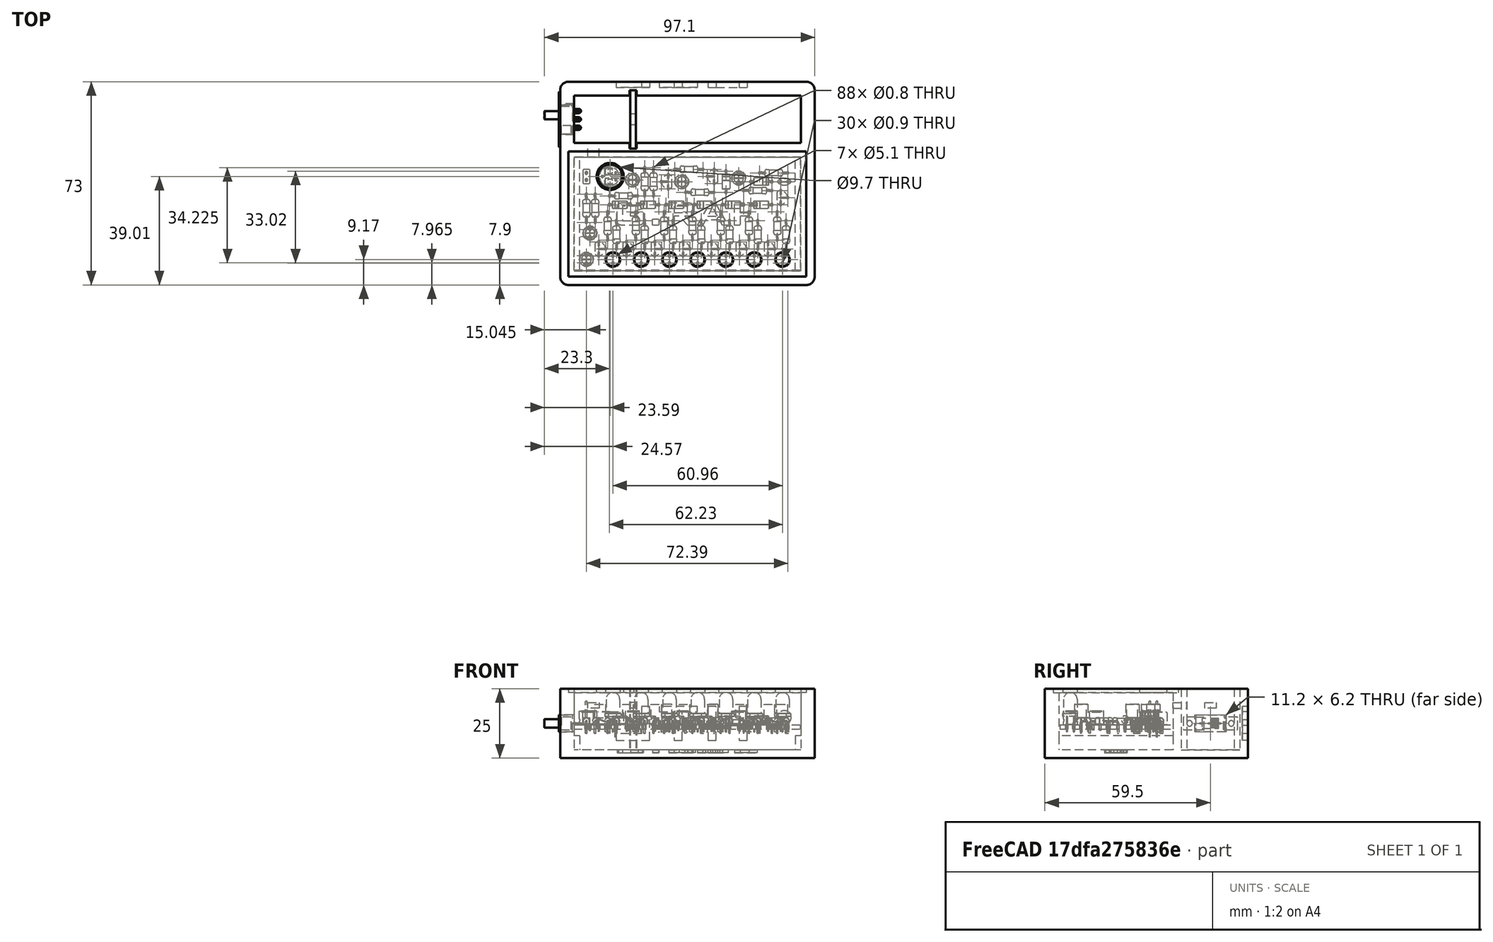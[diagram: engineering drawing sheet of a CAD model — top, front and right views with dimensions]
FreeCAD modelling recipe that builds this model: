
FCSTD DOCUMENT  (FreeCAD 0.20R29177 +426 (Git))
Label: housing
License: All rights reserved
LicenseURL: http://en.wikipedia.org/wiki/All_rights_reserved
objects: Part::Feature×64, TechDraw::DrawViewDimension×22, Sketcher::SketchObject×12, PartDesign::Pocket×10, App::Part×9, App::DocumentObjectGroupPython×4, PartDesign::Pad×3, PartDesign::Body×3, TechDraw::DrawSVGTemplate×3, TechDraw::DrawPage×3, TechDraw::DrawProjGroupItem×3, Part::Part2DObjectPython×2, TechDraw::DrawViewSpreadsheet×2, TechDraw::DrawViewPart×2, Spreadsheet::Sheet×1, TechDraw::DrawProjGroup×1, PartDesign::CoordinateSystem×1
note: 108 computed .brp shape members not serialized (recipe doc carries the construction recipe); baked Part::Feature solids carry a one-line shape summary decoded from their .brp

FEATURE [Spreadsheet::Sheet] Spreadsheet  label="Parameter"
  cells = A1=Board_Width; B1(Board_Width)=81.5; C1(Board_Length)=41; F1=Size; A2=Battery_Size; B2(Battery_Size)=17; E2=2AA_V; F2=16.5; A3=Height; B3(Height)=25; E3=2AA_H; F3=26; A4=Border; B4(Border)=5; E4=6AA_V; F4=47.5; A5=Border_Radius; B5(Border_Radius)=3; E5=6AA_H; F5=37.5; A6=Offset; B6(Offset)=-12; E6=6AAA_V; F6=26.2; A7=Overlay; B7(Overlay_Width)=2; C7(Overlay_Length)=0; E7=6AAA_H; F7=37.5; A8=Floor_Thickness; B8(Floor_Thickness)=3; E8=9VBLOCK_V; F8=17; A9=Base_Height; B9(Base_Height)=5; E9=9V_BLOCK_H; F9=26; A10=Inlay_Frame; B10(Inlay_Frame)=2; E10=Manual; F10=10; A11=Inlay_Height; B11(Inlay_Height)=1.5; C11=DICK; A12=Power_Size; B12(Power_Width)=4; C12(Power_Length)=2; A13=Power_Position; B13(Power_X)=5; C13(Power_Y)=6; A14=Power_Separation; B14(Power_Separation)=20; C14(Power_Separation_Size)=2; D14=DICK; A15=Power_Tolerance; B15(Power_Tolerance)=0.5; A16=Switch_Size; B16(Switch_Width)=11.2; C16(Switch_Height)=6.2; A17=Switch_Position; B17(Switch_X)==Border + Battery_Size / 2 - Switch_Width / 2; C17(Switch_Y)==Height / 2 + Offset - Switch_Height / 2; A18=Text; B18(Text)=HTL; C18(Text_Size)==Board_Width * (1 - 0.4) / Text_Length > Height * (1 - 0.2) ? Height * (1 - 0.2) : Board_Width * (1 - 0.4) / Text_Length; D18(Text_Length)=3; E18=Zeichen; A19=Text_Position; B19(Text_X)==Board_Width / 2 + Text_Length / 2 * Text_Size; C19(Text_Y)==Height / 2 + Offset - Text_Height / 2; A20=Text_Height; B20(Text_Height)==0.747 * Text_Size; A21=Text_Author; B21(Text_Author)=G.RAF; C21(Text_Author_Size)==Board_Width * (1 - 0.6) / Text_Length > Board_Length * (1 - 0.4) ? Board_Length * (1 - 0.4) : Board_Width * (1 - 0.6) / Text_Length; D21(Text_Author_Length)=5; E21=Zeichen; A22=Text_Author_Position; B22(Text_Author_X)==Board_Width / 2 - Text_Author_Length / 2 * Text_Author_Size; C22(Text_Author_Y)==-Board_Length / 2 - Text_Author_Height / 2; A23=Text_Author_Size; B23(Text_Author_Height)==0.747 * Text_Author_Size
FEATURE [Sketcher::SketchObject] Sketch
  AttachmentOffset = pos=(0,0,-12) rot=(0,0,1;0rad)
  FullyConstrained = true
  MapMode = 5
  Placement = pos=(0,0,-12) rot=(0,0,1;0rad)
  Support = -> [XY_Plane001]
  expr: .AttachmentOffset.Base.z = <<Parameter>>.Offset
  expr: Constraints[14] = <<Parameter>>.Board_Width + 2 * <<Parameter>>.Border
  expr: Constraints[15] = <<Parameter>>.Board_Length + <<Parameter>>.Border
  expr: Constraints[19] = <<Parameter>>.Border_Radius
  expr: Constraints[6] = <<Parameter>>.Battery_Size + 2 * <<Parameter>>.Border
  expr: Constraints[7] = <<Parameter>>.Border
  sketch-geometry (8):
    g0: LineSegment StartX=-2 StartY=27 StartZ=0 EndX=83.5 EndY=27 EndZ=0
    g1: LineSegment StartX=86.5 StartY=24 StartZ=0 EndX=86.5 EndY=-43 EndZ=0
    g2: LineSegment StartX=83.5 StartY=-46 StartZ=0 EndX=-2 EndY=-46 EndZ=0
    g3: LineSegment StartX=-5 StartY=-43 StartZ=0 EndX=-5 EndY=24 EndZ=0
    g4: ArcOfCircle CenterX=-2 CenterY=24 CenterZ=0 NormalX=0 NormalY=0 NormalZ=1 AngleXU=0 Radius=3 StartAngle=1.5708 EndAngle=3.14159
    g5: ArcOfCircle CenterX=83.5 CenterY=24 CenterZ=0 NormalX=0 NormalY=0 NormalZ=1 AngleXU=0 Radius=3 StartAngle=1.508e-13 EndAngle=1.5708
    g6: ArcOfCircle CenterX=83.5 CenterY=-43 CenterZ=0 NormalX=0 NormalY=0 NormalZ=1 AngleXU=0 Radius=3 StartAngle=4.71239 EndAngle=6.28319
    g7: ArcOfCircle CenterX=-2 CenterY=-43 CenterZ=0 NormalX=0 NormalY=0 NormalZ=1 AngleXU=0 Radius=3 StartAngle=3.14159 EndAngle=4.71239
  constraints (20):
    c: Horizontal(g0)
    c: Horizontal(g2)
    c: Vertical(g1)
    c: Vertical(g3)
    c: Tangent(g0,g4) = 1.5708
    c: Tangent(g3,g4) = 1.5708
    c: DistanceY(g-1,g0) = 27
    c: DistanceX(g3,g-1) = 5
    c: Tangent(g0,g5) = 1.5708
    c: Tangent(g1,g5) = 1.5708
    c: Tangent(g1,g6) = 1.5708
    c: Tangent(g2,g6) = 1.5708
    c: Tangent(g2,g7) = 1.5708
    c: Tangent(g3,g7) = 1.5708
    c: DistanceX(g3,g1) = 91.5
    c: DistanceY(g2,g-1) = 46
    c: Equal(g4,g5)
    c: Equal(g5,g6)
    c: Equal(g6,g7)
    c: Radius(g4) = 3
FEATURE [PartDesign::Pad] Pad
  Direction = (0,0,1)
  Length = 25
  Length2 = 10
  Profile = -> Sketch
  ReferenceAxis = -> Sketch [N_Axis]
  Type = 0
  expr: Length = <<Parameter>>.Height
FEATURE [Sketcher::SketchObject] Sketch001
  AttachmentOffset = pos=(0,0,13) rot=(0,0,1;0rad)
  FullyConstrained = true
  MapMode = 5
  Placement = pos=(0,0,13) rot=(0,0,1;0rad)
  Support = -> [XY_Plane001]
  expr: .AttachmentOffset.Base.z = <<Parameter>>.Height + <<Parameter>>.Offset
  expr: .AttachmentOffset.Rotation.Yaw = 0
  expr: Constraints[10] = <<Parameter>>.Overlay_Width
  expr: Constraints[11] = <<Parameter>>.Board_Width - 2 * <<Parameter>>.Overlay_Width
  expr: Constraints[21] = <<Parameter>>.Border
  expr: Constraints[22] = <<Parameter>>.Battery_Size
  expr: Constraints[23] = <<Parameter>>.Board_Width
  expr: Constraints[8] = <<Parameter>>.Overlay_Length
  expr: Constraints[9] = <<Parameter>>.Board_Length - 2 * <<Parameter>>.Overlay_Length
  sketch-geometry (8):
    g0: LineSegment StartX=2 StartY=0 StartZ=0 EndX=79.5 EndY=0 EndZ=0
    g1: LineSegment StartX=79.5 StartY=0 StartZ=0 EndX=79.5 EndY=-41 EndZ=0
    g2: LineSegment StartX=79.5 StartY=-41 StartZ=0 EndX=2 EndY=-41 EndZ=0
    g3: LineSegment StartX=2 StartY=-41 StartZ=0 EndX=2 EndY=0 EndZ=0
    g4: LineSegment StartX=0 StartY=22 StartZ=0 EndX=81.5 EndY=22 EndZ=0
    g5: LineSegment StartX=81.5 StartY=22 StartZ=0 EndX=81.5 EndY=5 EndZ=0
    g6: LineSegment StartX=81.5 StartY=5 StartZ=0 EndX=0 EndY=5 EndZ=0
    g7: LineSegment StartX=0 StartY=5 StartZ=0 EndX=0 EndY=22 EndZ=0
  constraints (24):
    c: Coincident(g0,g1)
    c: Coincident(g1,g2)
    c: Coincident(g2,g3)
    c: Coincident(g3,g0)
    c: Horizontal(g0)
    c: Horizontal(g2)
    c: Vertical(g1)
    c: Vertical(g3)
    c: DistanceY(g0,g-1) = 0
    c: DistanceY(g3,g3) = 41
    c: DistanceX(g-1,g0) = 2
    c: DistanceX(g0,g0) = 77.5
    c: Coincident(g4,g5)
    c: Coincident(g5,g6)
    c: Coincident(g6,g7)
    c: Coincident(g7,g4)
    c: Horizontal(g4)
    c: Horizontal(g6)
    c: Vertical(g5)
    c: Vertical(g7)
    c: PointOnObject(g4,g-2)
    c: DistanceY(g-1,g6) = 5
    c: DistanceY(g6,g4) = 17
    c: DistanceX(g4,g4) = 81.5
FEATURE [PartDesign::Pocket] Pocket
  BaseFeature = -> Pad
  Direction = (0,0,-1)
  Length = 22
  Length2 = 5
  Profile = -> Sketch001
  ReferenceAxis = -> Sketch001 [N_Axis]
  Type = 0
  expr: Length = <<Parameter>>.Height - <<Parameter>>.Floor_Thickness
FEATURE [Sketcher::SketchObject] Sketch002
  AttachmentOffset = pos=(0,0,13) rot=(0,0,1;0rad)
  FullyConstrained = true
  MapMode = 5
  Placement = pos=(0,0,13) rot=(0,0,1;0rad)
  Support = -> [XY_Plane001]
  expr: .AttachmentOffset.Base.z = <<Parameter>>.Height + <<Parameter>>.Offset
  expr: Constraints[10] = <<Parameter>>.Board_Length
  expr: Constraints[9] = <<Parameter>>.Board_Width
  sketch-geometry (4):
    g0: LineSegment StartX=0 StartY=0 StartZ=0 EndX=81.5 EndY=0 EndZ=0
    g1: LineSegment StartX=81.5 StartY=0 StartZ=0 EndX=81.5 EndY=-41 EndZ=0
    g2: LineSegment StartX=81.5 StartY=-41 StartZ=0 EndX=0 EndY=-41 EndZ=0
    g3: LineSegment StartX=0 StartY=-41 StartZ=0 EndX=0 EndY=0 EndZ=0
  constraints (11):
    c: Coincident(g0,g1)
    c: Coincident(g1,g2)
    c: Coincident(g2,g3)
    c: Coincident(g3,g0)
    c: Horizontal(g0)
    c: Horizontal(g2)
    c: Vertical(g1)
    c: Vertical(g3)
    c: Coincident(g0,g-1)
    c: DistanceX(g0,g0) = 81.5
    c: DistanceY(g3,g3) = 41
FEATURE [PartDesign::Pocket] Pocket001
  BaseFeature = -> Pocket
  Direction = (0,0,-1)
  Length = 17
  Length2 = 5
  Profile = -> Sketch002
  ReferenceAxis = -> Sketch002 [N_Axis]
  Type = 0
  expr: Length = <<Parameter>>.Height - <<Parameter>>.Floor_Thickness - <<Parameter>>.Base_Height
FEATURE [Sketcher::SketchObject] Sketch003
  AttachmentOffset = pos=(0,0,13) rot=(0,0,1;0rad)
  FullyConstrained = true
  MapMode = 5
  Placement = pos=(0,0,13) rot=(0,0,1;0rad)
  Support = -> [XY_Plane001]
  expr: .AttachmentOffset.Base.z = <<Parameter>>.Height + <<Parameter>>.Offset
  expr: Constraints[10] = <<Parameter>>.Board_Length + 2 * <<Parameter>>.Inlay_Frame
  expr: Constraints[11] = <<Parameter>>.Board_Width + 2 * <<Parameter>>.Inlay_Frame
  expr: Constraints[8] = <<Parameter>>.Inlay_Frame
  expr: Constraints[9] = <<Parameter>>.Inlay_Frame
  sketch-geometry (4):
    g0: LineSegment StartX=-2 StartY=2 StartZ=0 EndX=83.5 EndY=2 EndZ=0
    g1: LineSegment StartX=83.5 StartY=2 StartZ=0 EndX=83.5 EndY=-43 EndZ=0
    g2: LineSegment StartX=83.5 StartY=-43 StartZ=0 EndX=-2 EndY=-43 EndZ=0
    g3: LineSegment StartX=-2 StartY=-43 StartZ=0 EndX=-2 EndY=2 EndZ=0
  constraints (12):
    c: Coincident(g0,g1)
    c: Coincident(g1,g2)
    c: Coincident(g2,g3)
    c: Coincident(g3,g0)
    c: Horizontal(g0)
    c: Horizontal(g2)
    c: Vertical(g1)
    c: Vertical(g3)
    c: DistanceX(g0,g-1) = 2
    c: DistanceY(g-1,g0) = 2
    c: DistanceY(g1,g0) = 45
    c: DistanceX(g2,g1) = 85.5
FEATURE [PartDesign::Pocket] Pocket002
  BaseFeature = -> Pocket001
  Direction = (0,0,-1)
  Length = 1.5
  Length2 = 5
  Profile = -> Sketch003
  ReferenceAxis = -> Sketch003 [N_Axis]
  Refine = true
  Type = 0
  expr: Length = <<Parameter>>.Inlay_Height
FEATURE [Sketcher::SketchObject] Sketch004
  FullyConstrained = true
  MapMode = 5
  Placement = pos=(0,0,0) rot=(1,0,0;1.5708rad)
  Support = -> [XZ_Plane001]
  expr: Constraints[10] = <<Parameter>>.Power_Length
  expr: Constraints[11] = <<Parameter>>.Power_Width
  expr: Constraints[8] = <<Parameter>>.Power_X
  expr: Constraints[9] = <<Parameter>>.Power_Y
  sketch-geometry (4):
    g0: LineSegment StartX=5 StartY=8 StartZ=0 EndX=9 EndY=8 EndZ=0
    g1: LineSegment StartX=9 StartY=8 StartZ=0 EndX=9 EndY=6 EndZ=0
    g2: LineSegment StartX=9 StartY=6 StartZ=0 EndX=5 EndY=6 EndZ=0
    g3: LineSegment StartX=5 StartY=6 StartZ=0 EndX=5 EndY=8 EndZ=0
  constraints (12):
    c: Coincident(g0,g1)
    c: Coincident(g1,g2)
    c: Coincident(g2,g3)
    c: Coincident(g3,g0)
    c: Horizontal(g0)
    c: Horizontal(g2)
    c: Vertical(g1)
    c: Vertical(g3)
    c: DistanceX(g-1,g2) = 5
    c: DistanceY(g-1,g2) = 6
    c: DistanceY(g3,g3) = 2
    c: DistanceX(g0,g0) = 4
FEATURE [PartDesign::Pocket] Pocket003
  BaseFeature = -> Pocket002
  Direction = (0,1,2e-16)
  Length = 5
  Length2 = 5
  Profile = -> Sketch004
  ReferenceAxis = -> Sketch004 [N_Axis]
  Refine = true
  Type = 0
  expr: Length = <<Parameter>>.Border
FEATURE [Sketcher::SketchObject] Sketch005
  FullyConstrained = true
  MapMode = 5
  Placement = pos=(0,0,0) rot=(0.57735,0.57735,0.57735;2.0944rad)
  Support = -> [YZ_Plane001]
  expr: Constraints[10] = <<Parameter>>.Switch_X
  expr: Constraints[11] = <<Parameter>>.Switch_Y
  expr: Constraints[8] = <<Parameter>>.Switch_Width
  expr: Constraints[9] = <<Parameter>>.Switch_Height
  sketch-geometry (4):
    g0: LineSegment StartX=7.9 StartY=3.6 StartZ=0 EndX=19.1 EndY=3.6 EndZ=0
    g1: LineSegment StartX=19.1 StartY=3.6 StartZ=0 EndX=19.1 EndY=-2.6 EndZ=0
    g2: LineSegment StartX=19.1 StartY=-2.6 StartZ=0 EndX=7.9 EndY=-2.6 EndZ=0
    g3: LineSegment StartX=7.9 StartY=-2.6 StartZ=0 EndX=7.9 EndY=3.6 EndZ=0
  constraints (12):
    c: Coincident(g0,g1)
    c: Coincident(g1,g2)
    c: Coincident(g2,g3)
    c: Coincident(g3,g0)
    c: Horizontal(g0)
    c: Horizontal(g2)
    c: Vertical(g1)
    c: Vertical(g3)
    c: DistanceX(g0,g0) = 11.2
    c: DistanceY(g1,g1) = 6.2
    c: DistanceX(g-1,g2) = 7.9
    c: DistanceY(g-1,g2) = -2.6
FEATURE [PartDesign::Pocket] Pocket004
  BaseFeature = -> Pocket003
  Direction = (-1,2e-16,-3e-16)
  Length = 5
  Length2 = 5
  Profile = -> Sketch005
  ReferenceAxis = -> Sketch005 [N_Axis]
  Refine = true
  Type = 0
  expr: Length = <<Parameter>>.Border
FEATURE [Sketcher::SketchObject] Sketch006
  AttachmentOffset = pos=(0,0,13) rot=(0,0,1;0rad)
  FullyConstrained = true
  MapMode = 5
  Placement = pos=(0,0,13) rot=(0,0,1;0rad)
  Support = -> [XY_Plane001]
  expr: .AttachmentOffset.Base.z = <<Parameter>>.Height + <<Parameter>>.Offset
  expr: .AttachmentOffset.Rotation.Yaw = 0
  expr: Constraints[10] = <<Parameter>>.Battery_Size + 2 * <<Parameter>>.Power_Separation_Size
  expr: Constraints[11] = <<Parameter>>.Border - <<Parameter>>.Power_Separation_Size
  expr: Constraints[8] = <<Parameter>>.Power_Separation
  expr: Constraints[9] = <<Parameter>>.Power_Separation_Size + <<Parameter>>.Power_Tolerance
  sketch-geometry (4):
    g0: LineSegment StartX=20 StartY=24 StartZ=0 EndX=22.5 EndY=24 EndZ=0
    g1: LineSegment StartX=22.5 StartY=24 StartZ=0 EndX=22.5 EndY=3 EndZ=0
    g2: LineSegment StartX=22.5 StartY=3 StartZ=0 EndX=20 EndY=3 EndZ=0
    g3: LineSegment StartX=20 StartY=3 StartZ=0 EndX=20 EndY=24 EndZ=0
  constraints (12):
    c: Coincident(g0,g1)
    c: Coincident(g1,g2)
    c: Coincident(g2,g3)
    c: Coincident(g3,g0)
    c: Horizontal(g0)
    c: Horizontal(g2)
    c: Vertical(g1)
    c: Vertical(g3)
    c: DistanceX(g-1,g2) = 20
    c: DistanceX(g2,g2) = 2.5
    c: DistanceY(g1,g1) = 21
    c: DistanceY(g-1,g2) = 3
FEATURE [PartDesign::Pocket] Pocket005
  BaseFeature = -> Pocket004
  Direction = (0,0,-1)
  Length = 22
  Length2 = 5
  Profile = -> Sketch006
  ReferenceAxis = -> Sketch006 [N_Axis]
  Refine = true
  Type = 0
  expr: Length = <<Parameter>>.Height - <<Parameter>>.Floor_Thickness
FEATURE [Sketcher::SketchObject] Sketch007
  AttachmentOffset = pos=(0,0,13) rot=(0,0,1;0rad)
  FullyConstrained = true
  MapMode = 5
  Placement = pos=(0,0,13) rot=(0,0,1;0rad)
  Support = -> [XY_Plane003]
  expr: .AttachmentOffset.Base.z = <<Parameter>>.Height + <<Parameter>>.Offset
  expr: Constraints[10] = <<Parameter>>.Board_Width + 2 * <<Parameter>>.Inlay_Frame
  expr: Constraints[11] = <<Parameter>>.Board_Length + 2 * <<Parameter>>.Inlay_Frame
  expr: Constraints[8] = <<Parameter>>.Inlay_Frame
  expr: Constraints[9] = <<Parameter>>.Inlay_Frame
  sketch-geometry (4):
    g0: LineSegment StartX=-2 StartY=2 StartZ=0 EndX=83.5 EndY=2 EndZ=0
    g1: LineSegment StartX=83.5 StartY=2 StartZ=0 EndX=83.5 EndY=-43 EndZ=0
    g2: LineSegment StartX=83.5 StartY=-43 StartZ=0 EndX=-2 EndY=-43 EndZ=0
    g3: LineSegment StartX=-2 StartY=-43 StartZ=0 EndX=-2 EndY=2 EndZ=0
  constraints (12):
    c: Coincident(g0,g1)
    c: Coincident(g1,g2)
    c: Coincident(g2,g3)
    c: Coincident(g3,g0)
    c: Horizontal(g0)
    c: Horizontal(g2)
    c: Vertical(g1)
    c: Vertical(g3)
    c: DistanceX(g0,g-1) = 2
    c: DistanceY(g-1,g0) = 2
    c: DistanceX(g2,g1) = 85.5
    c: DistanceY(g1,g1) = 45
FEATURE [PartDesign::Pad] Pad001
  Direction = (0,0,1)
  Length = 1.5
  Length2 = 10
  Profile = -> Sketch007
  ReferenceAxis = -> Sketch007 [N_Axis]
  Refine = true
  Reversed = true
  Type = 0
  expr: Length = <<Parameter>>.Inlay_Height
FEATURE [Sketcher::SketchObject] Sketch008
  AttachmentOffset = pos=(0,0,13) rot=(0,0,1;0rad)
  FullyConstrained = true
  MapMode = 5
  Placement = pos=(0,0,13) rot=(0,0,1;0rad)
  Support = -> [XY_Plane005]
  expr: .AttachmentOffset.Base.z = <<Parameter>>.Height + <<Parameter>>.Offset
  expr: Constraints[10] = <<Parameter>>.Border - <<Parameter>>.Power_Separation_Size
  expr: Constraints[11] = <<Parameter>>.Battery_Size + 2 * <<Parameter>>.Power_Separation_Size
  expr: Constraints[8] = <<Parameter>>.Power_Separation + <<Parameter>>.Power_Tolerance / 2
  expr: Constraints[9] = <<Parameter>>.Power_Separation_Size
  sketch-geometry (4):
    g0: LineSegment StartX=20.25 StartY=24 StartZ=0 EndX=22.25 EndY=24 EndZ=0
    g1: LineSegment StartX=22.25 StartY=24 StartZ=0 EndX=22.25 EndY=3 EndZ=0
    g2: LineSegment StartX=22.25 StartY=3 StartZ=0 EndX=20.25 EndY=3 EndZ=0
    g3: LineSegment StartX=20.25 StartY=3 StartZ=0 EndX=20.25 EndY=24 EndZ=0
  constraints (12):
    c: Coincident(g0,g1)
    c: Coincident(g1,g2)
    c: Coincident(g2,g3)
    c: Coincident(g3,g0)
    c: Horizontal(g0)
    c: Horizontal(g2)
    c: Vertical(g1)
    c: Vertical(g3)
    c: DistanceX(g-1,g2) = 20.25
    c: DistanceX(g2,g2) = 2
    c: DistanceY(g-1,g2) = 3
    c: DistanceY(g1,g1) = 21
FEATURE [PartDesign::Pad] Pad002
  Direction = (0,0,1)
  Length = 22
  Length2 = 10
  Profile = -> Sketch008
  ReferenceAxis = -> Sketch008 [N_Axis]
  Refine = true
  Reversed = true
  Type = 0
  expr: Length = <<Parameter>>.Height - <<Parameter>>.Floor_Thickness
FEATURE [Sketcher::SketchObject] Sketch009
  AttachmentOffset = pos=(0,0,22) rot=(0,0,1;0rad)
  FullyConstrained = true
  MapMode = 5
  Placement = pos=(22,-4.9e-15,4.9e-15) rot=(0.57735,0.57735,0.57735;2.0944rad)
  Support = -> [YZ_Plane005]
  expr: .AttachmentOffset.Base.z = <<Parameter>>.Power_Separation + <<Parameter>>.Power_Separation_Size
  expr: Constraints[10] = <<Parameter>>.Power_Y
  expr: Constraints[11] = <<Parameter>>.Border + <<Parameter>>.Battery_Size / 2 - <<Parameter>>.Power_Width / 2
  expr: Constraints[8] = <<Parameter>>.Power_Width
  expr: Constraints[9] = <<Parameter>>.Power_Length
  sketch-geometry (4):
    g0: LineSegment StartX=11.5 StartY=8 StartZ=0 EndX=15.5 EndY=8 EndZ=0
    g1: LineSegment StartX=15.5 StartY=8 StartZ=0 EndX=15.5 EndY=6 EndZ=0
    g2: LineSegment StartX=15.5 StartY=6 StartZ=0 EndX=11.5 EndY=6 EndZ=0
    g3: LineSegment StartX=11.5 StartY=6 StartZ=0 EndX=11.5 EndY=8 EndZ=0
  constraints (12):
    c: Coincident(g0,g1)
    c: Coincident(g1,g2)
    c: Coincident(g2,g3)
    c: Coincident(g3,g0)
    c: Horizontal(g0)
    c: Horizontal(g2)
    c: Vertical(g1)
    c: Vertical(g3)
    c: DistanceX(g0,g0) = 4
    c: DistanceY(g1,g1) = 2
    c: DistanceY(g-1,g2) = 6
    c: DistanceX(g-1,g2) = 11.5
FEATURE [PartDesign::Pocket] Pocket006
  BaseFeature = -> Pad002
  Direction = (-1,2e-16,-3e-16)
  Length = 2
  Length2 = 5
  Profile = -> Sketch009
  ReferenceAxis = -> Sketch009 [N_Axis]
  Refine = true
  Type = 0
  expr: Length = <<Parameter>>.Power_Separation_Size
FEATURE [PartDesign::Body] Body002  label="Separator"
  Group = -> [Sketch008,Pad002,Sketch009,Pocket006]
  Origin = -> Origin005
  Tip = -> Pocket006
FEATURE [App::Part] Part002  label="Part_Separation"
  Group = -> [Body002]
  Origin = -> Origin004
FEATURE [Part::Part2DObjectPython] ShapeString  label="ShapeStringText"  # Draft 2D object (typed FeaturePython)
  FontFile = <path>
  MakeFace = true
  Placement = pos=(65.2,27,-5.58805) rot=(0,0.707107,0.707107;3.14159rad)
  Size = 16.3
  String = HTL
  Tracking = 0
  expr: .Placement.Base.x = <<Parameter>>.Text_X
  expr: .Placement.Base.y = <<Parameter>>.Battery_Size + 2 * <<Parameter>>.Border
  expr: .Placement.Base.z = <<Parameter>>.Text_Y
  expr: Size = <<Parameter>>.Text_Size
  expr: String = <<Parameter>>.Text
FEATURE [PartDesign::Pocket] Pocket007
  BaseFeature = -> Pocket005
  Direction = (0,-1,2e-16)
  Length = 2
  Length2 = 5
  Profile = -> ShapeString
  ReferenceAxis = -> ShapeString [N_Axis]
  Refine = true
  Type = 0
FEATURE [Part::Feature] Part__Feature  label="Switch"
  Placement = pos=(-3,13.5,0.5) rot=(0,0,1;1.5708rad)
  shape: bbox 13.1 x 19.5 x 6 mm, 88 faces (baked)
  expr: .Placement.Base.x = <<Parameter>>.Border - 8
  expr: .Placement.Base.y = <<Parameter>>.Border + <<Parameter>>.Battery_Size / 2
  expr: .Placement.Base.z = <<Parameter>>.Switch_Y + <<Parameter>>.Switch_Height / 2
FEATURE [App::Part] Part003  label="Part_Switch"
  Group = -> [Part__Feature]
  Origin = -> Origin006
FEATURE [Part::Feature] _VBlock  label="9VBlock"
  Placement = pos=(81.5,5,-9) rot=(0,0.707107,0.707107;3.14159rad)
  shape: bbox 47.82 x 17.05 x 27 mm, 433 faces, 0 solids (baked)
  expr: .Placement.Base.x = <<Parameter>>.Board_Width
  expr: .Placement.Base.y = <<Parameter>>.Border
  expr: .Placement.Base.z = <<Parameter>>.Offset + <<Parameter>>.Floor_Thickness
FEATURE [Part::Feature] AABlock
  Placement = pos=(81.5,5,33) rot=(0,1,0;3.14159rad)
  shape: bbox 60.2 x 28 x 46.2 mm, 481 faces, 0 solids (baked)
  expr: .Placement.Base.x = <<Parameter>>.Board_Width
  expr: .Placement.Base.y = <<Parameter>>.Border
  expr: .Placement.Base.z = <<Parameter>>.Height + <<Parameter>>.Floor_Thickness + 5
FEATURE [Part::Feature] AAABlock
  Placement = pos=(81.5,5,22) rot=(0,1,0;3.14159rad)
  shape: bbox 51 x 23 x 35.4 mm, 262 faces, 0 solids (baked)
  expr: .Placement.Base.x = <<Parameter>>.Board_Width
  expr: .Placement.Base.y = <<Parameter>>.Border
  expr: .Placement.Base.z = <<Parameter>>.Height - <<Parameter>>.Floor_Thickness
FEATURE [App::Part] Part004  label="Part_Battery"
  Group = -> [_VBlock,AABlock,AAABlock]
  Origin = -> Origin007
FEATURE [TechDraw::DrawSVGTemplate] Template
  EditableTexts = Designed_by_Name=GAR; Drawing_number=H0101; FC-Date=14.04.2023; FC-SC=1:1; FC-SH=01; FC-Title=Gehäuse; Subtitle=Vorlage; Weight=-
  Height = 210
  Orientation = 1
  Width = 297
FEATURE [TechDraw::DrawSVGTemplate] Template001
  EditableTexts = Designed_by_Name=GAR; Drawing_number=H0101; FC-Date=14.04.2023; FC-SC=1:1; FC-SH=02; FC-Title=Acrylglas; Subtitle=Vorlage; Weight=-
  Height = 210
  Orientation = 1
  Width = 297
FEATURE [TechDraw::DrawViewSpreadsheet] Sheet
  CellEnd = C11
  CellStart = B11
  Font = osifont
  LineWidth = 0.35
  LockPosition = false
  Rotation = 0
  ScaleType = 2
  Source = -> Spreadsheet
  Symbol = <svg\n	xmlns="http://www.w3.org/2000/svg" version="1.1"\n	xmlns:freecad="http://www.freecadweb.org/wiki/index.php?title=Svg_Namespace">\n<g id="Sheet">\n  <g id="Sheet_colB">\n    <rect x="0" y="0" width="100" height="30" style="fill:none;stroke-width:0.35;stroke:#000000;" />\n    <text style="" x="10" y="22.5" font-family="osifont" font-size="20" fill="#000000">1,50</text>\n  </g>\n  <g id="Sheet_colC">\n    <rect x="100" y="0" width="100" height="30" style="fill:none;stroke-width:0.35;stroke:#000000;" />\n    <text style="" x="110" y="22.5" font-family="osifont" font-size="20" fill="#000000">DICK</text>\n  </g>\n</g>\n\n</svg>
  TextSize = 20
  X = 238.264
  Y = 136.617
FEATURE [TechDraw::DrawSVGTemplate] Template002
  EditableTexts = Designed_by_Name=GAR; Drawing_number=H0101; FC-Date=14.04.2023; FC-SC=1:2; FC-SH=03; FC-Title=Trennblech; Subtitle=Vorlage; Weight=-
  Height = 210
  Orientation = 1
  Width = 297
FEATURE [TechDraw::DrawViewPart] View001
  CoarseView = false
  Direction = (-1,0,0)
  Focus = 100
  HardHidden = false
  IsoCount = 0
  IsoHidden = false
  IsoVisible = false
  LockPosition = false
  Perspective = false
  Rotation = 0
  Scale = 2
  ScaleType = 0
  SeamHidden = false
  SeamVisible = true
  SmoothHidden = false
  SmoothVisible = true
  Source = -> [Part002]
  X = 150.491
  XDirection = (0,-1,0)
  Y = 126.564
FEATURE [TechDraw::DrawViewDimension] Dimension
  AngleOverride = false
  Arbitrary = false
  ArbitraryTolerances = false
  EqualTolerance = true
  ExtensionAngle = 0
  FormatSpec = %.2w
  FormatSpecOverTolerance = %+.2w
  FormatSpecUnderTolerance = %+.2w
  Inverted = false
  LineAngle = 0
  LockPosition = false
  MeasureType = 1
  OverTolerance = 0
  References2D = -> [View001]
  Rotation = 0
  Scale = 2
  ScaleType = 0
  TheoreticalExact = false
  Type = 2
  UnderTolerance = 0
  X = -36.3703
  Y = 2.21412
FEATURE [TechDraw::DrawViewDimension] Dimension014
  AngleOverride = false
  Arbitrary = false
  ArbitraryTolerances = false
  EqualTolerance = true
  ExtensionAngle = 0
  FormatSpec = %.2w
  FormatSpecOverTolerance = %+.2w
  FormatSpecUnderTolerance = %+.2w
  Inverted = false
  LineAngle = 0
  LockPosition = false
  MeasureType = 1
  OverTolerance = 0
  References2D = -> [View001]
  Rotation = 0
  Scale = 2
  ScaleType = 0
  TheoreticalExact = false
  Type = 1
  UnderTolerance = 0
  X = -1.32701
  Y = 42.5096
FEATURE [TechDraw::DrawViewDimension] Dimension015
  AngleOverride = false
  Arbitrary = false
  ArbitraryTolerances = false
  EqualTolerance = true
  ExtensionAngle = 0
  FormatSpec = %.2w
  FormatSpecOverTolerance = %+.2w
  FormatSpecUnderTolerance = %+.2w
  Inverted = false
  LineAngle = 0
  LockPosition = false
  MeasureType = 1
  OverTolerance = 0
  References2D = -> [View001]
  Rotation = 0
  Scale = 2
  ScaleType = 0
  TheoreticalExact = false
  Type = 1
  UnderTolerance = 0
  X = -11.6638
  Y = 1.00042
FEATURE [TechDraw::DrawViewDimension] Dimension016
  AngleOverride = false
  Arbitrary = false
  ArbitraryTolerances = false
  EqualTolerance = true
  ExtensionAngle = 0
  FormatSpec = %.2w
  FormatSpecOverTolerance = %+.2w
  FormatSpecUnderTolerance = %+.2w
  Inverted = false
  LineAngle = 0
  LockPosition = false
  MeasureType = 1
  OverTolerance = 0
  References2D = -> [View001]
  Rotation = 0
  Scale = 2
  ScaleType = 0
  TheoreticalExact = false
  Type = 2
  UnderTolerance = 0
  X = 9.31345
  Y = 5.13137
FEATURE [TechDraw::DrawViewDimension] Dimension017
  AngleOverride = false
  Arbitrary = false
  ArbitraryTolerances = false
  EqualTolerance = true
  ExtensionAngle = 0
  FormatSpec = %.2w
  FormatSpecOverTolerance = %+.2w
  FormatSpecUnderTolerance = %+.2w
  Inverted = false
  LineAngle = 0
  LockPosition = false
  MeasureType = 1
  OverTolerance = 0
  References2D = -> [View001]
  Rotation = 0
  Scale = 2
  ScaleType = 0
  TheoreticalExact = false
  Type = 2
  UnderTolerance = 0
  X = 30.2802
  Y = -7.52786
FEATURE [TechDraw::DrawViewDimension] Dimension018
  AngleOverride = false
  Arbitrary = false
  ArbitraryTolerances = false
  EqualTolerance = true
  ExtensionAngle = 0
  FormatSpec = %.2w
  FormatSpecOverTolerance = %+.2w
  FormatSpecUnderTolerance = %+.2w
  Inverted = false
  LineAngle = 0
  LockPosition = false
  MeasureType = 1
  OverTolerance = 0
  References2D = -> [View001]
  Rotation = 0
  Scale = 2
  ScaleType = 0
  TheoreticalExact = false
  Type = 1
  UnderTolerance = 0
  X = -13.8116
  Y = -29.6598
FEATURE [TechDraw::DrawViewSpreadsheet] Sheet001
  CellEnd = D14
  CellStart = C14
  Font = osifont
  LineWidth = 0.35
  LockPosition = false
  Rotation = 0
  ScaleType = 2
  Source = -> Spreadsheet
  Symbol = <svg\n	xmlns="http://www.w3.org/2000/svg" version="1.1"\n	xmlns:freecad="http://www.freecadweb.org/wiki/index.php?title=Svg_Namespace">\n<g id="Sheet001">\n  <g id="Sheet001_colC">\n    <rect x="0" y="0" width="100" height="30" style="fill:none;stroke-width:0.35;stroke:#000000;" />\n    <text style="" x="6" y="22.5" font-family="osifont" font-size="12" fill="#000000">2</text>\n  </g>\n  <g id="Sheet001_colD">\n    <rect x="100" y="0" width="100" height="30" style="fill:none;stroke-width:0.35;stroke:#000000;" />\n    <text style="" x="106" y="22.5" font-family="osifont" font-size="12" fill="#000000">DICK</text>\n  </g>\n</g>\n\n</svg>
  TextSize = 12
  X = 232.765
  Y = 120.261
FEATURE [TechDraw::DrawPage] Page002  label="Page_Separation"
  KeepUpdated = true
  NextBalloonIndex = 1
  ProjectionType = 0
  Scale = 2
  Template = -> Template002
  Views = -> [View001,Dimension,Dimension014,Dimension015,Dimension016,Dimension017,Dimension018,Sheet001]
FEATURE [Part::Part2DObjectPython] ShapeString001  label="ShapeStringAuthor"  # Draft 2D object (typed FeaturePython)
  FontFile = <path>
  MakeFace = true
  Placement = pos=(13.5833,-24.5587,-9) rot=(0,0,1;0rad)
  Size = 10.8667
  String = G.RAF
  Tracking = 0
  expr: .Placement.Base.x = <<Parameter>>.Text_Author_X
  expr: .Placement.Base.y = <<Parameter>>.Text_Author_Y
  expr: .Placement.Base.z = <<Parameter>>.Offset + <<Parameter>>.Floor_Thickness
  expr: Size = <<Parameter>>.Text_Author_Size
  expr: String = <<Parameter>>.Text_Author
FEATURE [PartDesign::Pocket] Pocket008
  BaseFeature = -> Pocket007
  Direction = (0,0,-1)
  Length = 1
  Length2 = 5
  Profile = -> ShapeString001
  ReferenceAxis = -> ShapeString001 [N_Axis]
  Refine = true
  Type = 0
FEATURE [PartDesign::Body] Body
  Group = -> [Sketch,Pad,Sketch001,Pocket,Sketch002,Pocket001,Sketch003,Pocket002,Sketch004,Pocket003,Sketch005,Pocket004,Sketch006,Pocket005,ShapeString,Pocket007,ShapeString001,Pocket008]
  Origin = -> Origin001
  Tip = -> Pocket008
FEATURE [App::Part] Part  label="Part_Case"
  Group = -> [Body]
  Origin = -> Origin
FEATURE [TechDraw::DrawProjGroupItem] ProjItem  label="Front"
  CoarseView = false
  Direction = (0,0,1)
  Focus = 100
  HardHidden = false
  IsoCount = 0
  IsoHidden = false
  IsoVisible = false
  LockPosition = true
  Perspective = false
  Rotation = 0
  RotationVector = (-1,0,0)
  ScaleType = 2
  SeamHidden = false
  SeamVisible = true
  SmoothHidden = false
  SmoothVisible = true
  Source = -> [Part]
  Type = 0
  X = 0
  XDirection = (1,1e-16,0)
  Y = 0
FEATURE [TechDraw::DrawProjGroupItem] ProjItem001  label="Right"
  CoarseView = false
  Direction = (1,1e-16,1e-16)
  Focus = 100
  HardHidden = false
  IsoCount = 0
  IsoHidden = false
  IsoVisible = false
  LockPosition = false
  Perspective = false
  Rotation = 0
  RotationVector = (1,0,0)
  ScaleType = 2
  SeamHidden = false
  SeamVisible = true
  SmoothHidden = false
  SmoothVisible = true
  Source = -> [Part]
  Type = 2
  X = 91.5
  XDirection = (1e-16,0,-1)
  Y = 0
FEATURE [TechDraw::DrawProjGroupItem] ProjItem002  label="Left"
  CoarseView = false
  Direction = (-1,-1e-16,1e-16)
  Focus = 100
  HardHidden = false
  IsoCount = 0
  IsoHidden = false
  IsoVisible = false
  LockPosition = false
  Perspective = false
  Rotation = 0
  RotationVector = (1,0,0)
  ScaleType = 2
  SeamHidden = false
  SeamVisible = true
  SmoothHidden = false
  SmoothVisible = true
  Source = -> [Part]
  Type = 1
  X = -91.5
  XDirection = (1e-16,0,1)
  Y = 0
FEATURE [TechDraw::DrawProjGroup] ProjGroup
  Anchor = -> ProjItem
  AutoDistribute = true
  LockPosition = false
  ProjectionType = 1
  Rotation = 0
  ScaleType = 0
  Source = -> [Part]
  Views = -> [ProjItem,ProjItem001,ProjItem002]
  X = 151.526
  Y = 127.757
  spacingX = 0
  spacingY = 5
FEATURE [TechDraw::DrawViewDimension] Dimension019
  AngleOverride = false
  Arbitrary = false
  ArbitraryTolerances = false
  EqualTolerance = true
  ExtensionAngle = 0
  FormatSpec = %.2w
  FormatSpecOverTolerance = %+.2w
  FormatSpecUnderTolerance = %+.2w
  Inverted = false
  LineAngle = 0
  LockPosition = false
  MeasureType = 1
  OverTolerance = 0
  References2D = -> [ProjItem002]
  Rotation = 0
  ScaleType = 0
  TheoreticalExact = false
  Type = 1
  UnderTolerance = 0
  X = 7.55496
  Y = 52.7971
FEATURE [TechDraw::DrawViewDimension] Dimension020
  AngleOverride = false
  Arbitrary = false
  ArbitraryTolerances = false
  EqualTolerance = true
  ExtensionAngle = 0
  FormatSpec = %.2w
  FormatSpecOverTolerance = %+.2w
  FormatSpecUnderTolerance = %+.2w
  Inverted = false
  LineAngle = 0
  LockPosition = false
  MeasureType = 1
  OverTolerance = 0
  References2D = -> [ProjItem002]
  Rotation = 0
  ScaleType = 0
  TheoreticalExact = false
  Type = 2
  UnderTolerance = 0
  X = -20.4648
  Y = 29.224
FEATURE [TechDraw::DrawViewDimension] Dimension021
  AngleOverride = false
  Arbitrary = false
  ArbitraryTolerances = false
  EqualTolerance = true
  ExtensionAngle = 0
  FormatSpec = %.2w
  FormatSpecOverTolerance = %+.2w
  FormatSpecUnderTolerance = %+.2w
  Inverted = false
  LineAngle = 0
  LockPosition = false
  MeasureType = 1
  OverTolerance = 0
  References2D = -> [ProjItem002]
  Rotation = 0
  ScaleType = 0
  TheoreticalExact = false
  Type = 1
  UnderTolerance = 0
  X = 7.10618
  Y = 16.5587
FEATURE [TechDraw::DrawViewDimension] Dimension022
  AngleOverride = false
  Arbitrary = false
  ArbitraryTolerances = false
  EqualTolerance = true
  ExtensionAngle = 0
  FormatSpec = %.2w
  FormatSpecOverTolerance = %+.2w
  FormatSpecUnderTolerance = %+.2w
  Inverted = false
  LineAngle = 0
  LockPosition = false
  MeasureType = 1
  OverTolerance = 0
  References2D = -> [ProjItem002]
  Rotation = 0
  ScaleType = 0
  TheoreticalExact = false
  Type = 2
  UnderTolerance = 0
  X = 21.4814
  Y = 39.279
FEATURE [TechDraw::DrawViewDimension] Dimension023
  AngleOverride = false
  Arbitrary = false
  ArbitraryTolerances = false
  EqualTolerance = true
  ExtensionAngle = 0
  FormatSpec = %.2w
  FormatSpecOverTolerance = %+.2w
  FormatSpecUnderTolerance = %+.2w
  Inverted = false
  LineAngle = 0
  LockPosition = false
  MeasureType = 1
  OverTolerance = 0
  References2D = -> [ProjItem001]
  Rotation = 0
  ScaleType = 0
  TheoreticalExact = false
  Type = 2
  UnderTolerance = 0
  X = -25.0267
  Y = 2.05259
FEATURE [TechDraw::DrawViewDimension] Dimension024
  AngleOverride = false
  Arbitrary = false
  ArbitraryTolerances = false
  EqualTolerance = true
  ExtensionAngle = 0
  FormatSpec = %.2w
  FormatSpecOverTolerance = %+.2w
  FormatSpecUnderTolerance = %+.2w
  Inverted = false
  LineAngle = 0
  LockPosition = false
  MeasureType = 1
  OverTolerance = 0
  References2D = -> [ProjItem001]
  Rotation = 0
  ScaleType = 0
  TheoreticalExact = false
  Type = 1
  UnderTolerance = 0
  X = -0.894763
  Y = 55.5134
FEATURE [TechDraw::DrawViewDimension] Dimension025
  AngleOverride = false
  Arbitrary = false
  ArbitraryTolerances = false
  EqualTolerance = true
  ExtensionAngle = 0
  FormatSpec = %.2w
  FormatSpecOverTolerance = %+.2w
  FormatSpecUnderTolerance = %+.2w
  Inverted = false
  LineAngle = 0
  LockPosition = false
  MeasureType = 1
  OverTolerance = 0
  References2D = -> [ProjItem]
  Rotation = 0
  ScaleType = 0
  TheoreticalExact = false
  Type = 1
  UnderTolerance = 0
  X = -21.1708
  Y = 8.67006
FEATURE [TechDraw::DrawViewDimension] Dimension026
  AngleOverride = false
  Arbitrary = false
  ArbitraryTolerances = false
  EqualTolerance = true
  ExtensionAngle = 0
  FormatSpec = %.2w
  FormatSpecOverTolerance = %+.2w
  FormatSpecUnderTolerance = %+.2w
  Inverted = false
  LineAngle = 0
  LockPosition = false
  MeasureType = 1
  OverTolerance = 0
  References2D = -> [ProjItem]
  Rotation = 0
  ScaleType = 0
  TheoreticalExact = false
  Type = 2
  UnderTolerance = 0
  X = -10.5521
  Y = 29.7763
FEATURE [TechDraw::DrawViewDimension] Dimension027
  AngleOverride = false
  Arbitrary = false
  ArbitraryTolerances = false
  EqualTolerance = true
  ExtensionAngle = 0
  FormatSpec = %.2w
  FormatSpecOverTolerance = %+.2w
  FormatSpecUnderTolerance = %+.2w
  Inverted = false
  LineAngle = 0
  LockPosition = false
  MeasureType = 1
  OverTolerance = 0
  References2D = -> [ProjItem]
  Rotation = 0
  ScaleType = 0
  TheoreticalExact = false
  Type = 2
  UnderTolerance = 0
  X = -21.2893
  Y = 29.7763
FEATURE [TechDraw::DrawViewDimension] Dimension028
  AngleOverride = false
  Arbitrary = false
  ArbitraryTolerances = false
  EqualTolerance = true
  ExtensionAngle = 0
  FormatSpec = %.2w
  FormatSpecOverTolerance = %+.2w
  FormatSpecUnderTolerance = %+.2w
  Inverted = false
  LineAngle = 0
  LockPosition = false
  MeasureType = 1
  OverTolerance = 0
  References2D = -> [ProjItem]
  Rotation = 0
  ScaleType = 0
  TheoreticalExact = false
  Type = 2
  UnderTolerance = 0
  X = 64.0176
  Y = 41.6922
FEATURE [TechDraw::DrawViewDimension] Dimension029
  AngleOverride = false
  Arbitrary = false
  ArbitraryTolerances = false
  EqualTolerance = true
  ExtensionAngle = 0
  FormatSpec = %.2w
  FormatSpecOverTolerance = %+.2w
  FormatSpecUnderTolerance = %+.2w
  Inverted = false
  LineAngle = 0
  LockPosition = false
  MeasureType = 1
  OverTolerance = 0
  References2D = -> [ProjItem]
  Rotation = 0
  ScaleType = 0
  TheoreticalExact = false
  Type = 1
  UnderTolerance = 0
  X = -42.1437
  Y = 33.9329
FEATURE [TechDraw::DrawViewDimension] Dimension030
  AngleOverride = false
  Arbitrary = false
  ArbitraryTolerances = false
  EqualTolerance = true
  ExtensionAngle = 0
  FormatSpec = %.2w
  FormatSpecOverTolerance = %+.2w
  FormatSpecUnderTolerance = %+.2w
  Inverted = false
  LineAngle = 0
  LockPosition = false
  MeasureType = 1
  OverTolerance = 0
  References2D = -> [ProjItem]
  Rotation = 0
  ScaleType = 0
  TheoreticalExact = false
  Type = 1
  UnderTolerance = 0
  X = -0.647253
  Y = 53.4628
FEATURE [TechDraw::DrawViewDimension] Dimension031
  AngleOverride = false
  Arbitrary = false
  ArbitraryTolerances = false
  EqualTolerance = true
  ExtensionAngle = 0
  FormatSpec = R%.2w
  FormatSpecOverTolerance = %+.2w
  FormatSpecUnderTolerance = %+.2w
  Inverted = false
  LineAngle = 0
  LockPosition = false
  MeasureType = 1
  OverTolerance = 0
  References2D = -> [ProjItem]
  Rotation = 0
  ScaleType = 0
  TheoreticalExact = false
  Type = 4
  UnderTolerance = 0
  X = -58.1596
  Y = 53.3129
FEATURE [TechDraw::DrawViewDimension] Dimension032
  AngleOverride = false
  Arbitrary = false
  ArbitraryTolerances = false
  EqualTolerance = true
  ExtensionAngle = 0
  FormatSpec = %.2w
  FormatSpecOverTolerance = %+.2w
  FormatSpecUnderTolerance = %+.2w
  Inverted = false
  LineAngle = 0
  LockPosition = false
  MeasureType = 1
  OverTolerance = 0
  References2D = -> [ProjItem]
  Rotation = 0
  ScaleType = 0
  TheoreticalExact = false
  Type = 1
  UnderTolerance = 0
  X = 52.552
  Y = 53.4287
FEATURE [TechDraw::DrawPage] Page  label="Page_Case"
  KeepUpdated = true
  NextBalloonIndex = 1
  ProjectionType = 0
  Template = -> Template
  Views = -> [ProjGroup,Dimension019,Dimension020,Dimension021,Dimension022,Dimension023,Dimension024,Dimension025,Dimension026,Dimension027,Dimension028,Dimension029,Dimension030,Dimension031,Dimension032]
FEATURE [PartDesign::CoordinateSystem] Local_CS_1d7d
  AttacherType = Attacher::AttachEngine3D
  MapMode = 2
  Support = -> [X_Axis009]
FEATURE [Part::Feature] Pcb_1d7d
  Placement = pos=(-95.25,69.85,0) rot=(0,0,1;0rad)
  shape: bbox 81.28 x 40.64 x 1.6 mm, 128 faces (baked)
FEATURE [Sketcher::SketchObject] PCB_Sketch_1d7d
  FullyConstrained = false
  sketch-geometry (4):
    g0: LineSegment StartX=0 StartY=0 StartZ=0 EndX=81.28 EndY=0 EndZ=0
    g1: LineSegment StartX=81.28 StartY=0 StartZ=0 EndX=81.28 EndY=-40.64 EndZ=0
    g2: LineSegment StartX=0 StartY=-40.64 StartZ=0 EndX=0 EndY=0 EndZ=0
    g3: LineSegment StartX=81.28 StartY=-40.64 StartZ=0 EndX=0 EndY=-40.64 EndZ=0
  constraints (4):
    c: Coincident(g2,g3)
    c: Coincident(g0,g2)
    c: Coincident(g1,g3)
    c: Coincident(g0,g1)
FEATURE [App::Part] Board_Geoms_1d7d
  Group = -> [Pcb_1d7d,PCB_Sketch_1d7d]
  Origin = -> Origin008
FEATURE [Part::Feature] Shape  label="Q7_TO-92_Wide_4bfbe9c5f8f4"
  Placement = pos=(8.89,-30.48,0) rot=(0,0,-1;1.5708rad)
  shape: bbox 4.06 x 5.62 x 9.8 mm, 31 faces (baked)
FEATURE [Part::Feature] Shape001  label="C6_C_Disc_D50mm_W25mm_P250mm_441e31f26d57"
  Placement = pos=(74.315,-8.89,0) rot=(0,0,1;0rad)
  shape: bbox 5 x 2.5 x 7.1 mm, 6 faces (baked)
FEATURE [Part::Feature] Shape002  label="D14_D_A-405_P7.62mm_Horizontal_84994ef9fd34"
  Placement = pos=(71.12,-8.89,0) rot=(0,0,1;3.14159rad)
  shape: bbox 8.368 x 2.72 x 5.71 mm, 15 faces (baked)
FEATURE [Part::Feature] Shape003  label="R22_R_Axial_DIN0207_L63mm_D25mm_P1016mm_Horizontal_d8874ca5abab"
  Placement = pos=(36.195,-4.445,0) rot=(0,0,1;0rad)
  shape: bbox 10.96 x 2.706 x 5.603 mm, 17 faces (baked)
FEATURE [Part::Feature] Shape004  label="R15_R_Axial_DIN0207_L63mm_D25mm_P1016mm_Horizontal_26bb8defbff6"
  Placement = pos=(71.12,-12.065,0) rot=(0,0,1;3.14159rad)
  shape: bbox 10.96 x 2.706 x 5.603 mm, 17 faces (baked)
FEATURE [Part::Feature] Shape005  label="D3_LED_D5.0mm_3ee2d2edeb13"
  Placement = pos=(54.61,-35.555,0) rot=(0,0,-1;1.5708rad)
  shape: bbox 5.8 x 5.4 x 14.1 mm, 16 faces (baked)
FEATURE [Part::Feature] Shape006  label="Q8_TO-92_Wide_a93fba4ea393"
  Placement = pos=(74.295,-12.065,0) rot=(0,0,-1;1.5708rad)
  shape: bbox 4.06 x 5.62 x 9.8 mm, 31 faces (baked)
FEATURE [Part::Feature] Shape007  label="Q1_TO-92_Wide_c0447f71f260"
  Placement = pos=(69.635,-30.47,0) rot=(0,0,-1;1.5708rad)
  shape: bbox 4.06 x 5.62 x 9.8 mm, 31 faces (baked)
FEATURE [Part::Feature] Shape008  label="D4_LED_D5.0mm_dc1b8127458c"
  Placement = pos=(44.45,-35.56,0) rot=(0,0,-1;1.5708rad)
  shape: bbox 5.8 x 5.4 x 14.1 mm, 16 faces (baked)
FEATURE [Part::Feature] Shape009  label="Q9_TO-92_Wide_263e551227a1"
  Placement = pos=(50.38,-9.535,0) rot=(0,0,1;1.5708rad)
  shape: bbox 4.06 x 5.62 x 9.8 mm, 31 faces (baked)
FEATURE [Part::Feature] Shape010  label="R14_R_Axial_DIN0207_L63mm_D25mm_P1016mm_Horizontal_b1f9f71ed35f"
  Placement = pos=(12.065,-29.845,0) rot=(0,0,1;1.5708rad)
  shape: bbox 2.706 x 10.96 x 5.603 mm, 17 faces (baked)
FEATURE [Part::Feature] Shape011  label="R13_R_Axial_DIN0207_L63mm_D25mm_P1016mm_Horizontal_caadc2475899"
  Placement = pos=(22.225,-29.845,0) rot=(0,0,1;1.5708rad)
  shape: bbox 2.706 x 10.96 x 5.603 mm, 17 faces (baked)
FEATURE [Part::Feature] Shape012  label="R8_R_Axial_DIN0207_L63mm_D25mm_P1016mm_Horizontal_83ed933a83d2"
  Placement = pos=(73.025,-29.845,0) rot=(0,0,1;1.5708rad)
  shape: bbox 2.706 x 10.96 x 5.603 mm, 17 faces (baked)
FEATURE [Part::Feature] Shape013  label="R2_R_Axial_DIN0207_L63mm_D25mm_P1016mm_Horizontal_2cb8f415b4d6"
  Placement = pos=(66.04,-22.86,0) rot=(0,0,-1;1.5708rad)
  shape: bbox 2.706 x 10.96 x 5.603 mm, 17 faces (baked)
FEATURE [Part::Feature] Shape014  label="R1_R_Axial_DIN0207_L63mm_D25mm_P1016mm_Horizontal_401779ecf60e"
  Placement = pos=(76.2,-22.86,0) rot=(0,0,-1;1.5708rad)
  shape: bbox 2.706 x 10.96 x 5.603 mm, 17 faces (baked)
FEATURE [Part::Feature] Shape015  label="MK1_CUI_DEVICES_CMA-4544PF-W_7a05e5a25c01"
  Placement = pos=(12.986,-6.985,0) rot=(1,0,0;1.5708rad)
  shape: bbox 10.5 x 10.5 x 9.2 mm, 56 faces (baked)
FEATURE [Part::Feature] Shape016  label="D15_D_A-405_P7.62mm_Horizontal_00f129ff81aa"
  Placement = pos=(54.61,-5.08,0) rot=(0,0,-1;1.5708rad)
  shape: bbox 2.72 x 8.368 x 5.71 mm, 15 faces (baked)
FEATURE [Part::Feature] Shape017  label="D12_D_A-405_P7.62mm_Horizontal_3dac00b416f9"
  Placement = pos=(22.86,-17.145,0) rot=(0,0,1;0rad)
  shape: bbox 8.368 x 2.72 x 5.71 mm, 15 faces (baked)
FEATURE [Part::Feature] Shape018  label="Q5_TO-92_Wide_fe35382576d2"
  Placement = pos=(28.995,-30.47,0) rot=(0,0,-1;1.5708rad)
  shape: bbox 4.06 x 5.62 x 9.8 mm, 31 faces (baked)
FEATURE [Part::Feature] Shape019  label="Q6_TO-92_Wide_d52b6dc564fe"
  Placement = pos=(18.835,-30.47,0) rot=(0,0,-1;1.5708rad)
  shape: bbox 4.06 x 5.62 x 9.8 mm, 31 faces (baked)
FEATURE [Part::Feature] Shape020  label="R12_R_Axial_DIN0207_L63mm_D25mm_P1016mm_Horizontal_3b9f8811e661"
  Placement = pos=(32.385,-29.845,0) rot=(0,0,1;1.5708rad)
  shape: bbox 2.706 x 10.96 x 5.603 mm, 17 faces (baked)
FEATURE [Part::Feature] Shape021  label="D11_D_A-405_P7.62mm_Horizontal_5c6651d95b19"
  Placement = pos=(33.02,-17.145,0) rot=(0,0,1;0rad)
  shape: bbox 8.368 x 2.72 x 5.71 mm, 15 faces (baked)
FEATURE [Part::Feature] Shape022  label="R3_R_Axial_DIN0207_L63mm_D25mm_P1016mm_Horizontal_a9c3d9380691"
  Placement = pos=(55.88,-22.86,0) rot=(0,0,-1;1.5708rad)
  shape: bbox 2.706 x 10.96 x 5.603 mm, 17 faces (baked)
FEATURE [Part::Feature] Shape023  label="D6_LED_D5.0mm_595b68b19a06"
  Placement = pos=(24.13,-35.555,0) rot=(0,0,-1;1.5708rad)
  shape: bbox 5.8 x 5.4 x 14.1 mm, 16 faces (baked)
FEATURE [Part::Feature] Shape024  label="R20_R_Axial_DIN0207_L63mm_D25mm_P1016mm_Horizontal_8b5b8a0e60e4"
  Placement = pos=(7.62,-13.335,0) rot=(0,0,-1;1.5708rad)
  shape: bbox 2.706 x 10.96 x 5.603 mm, 17 faces (baked)
FEATURE [Part::Feature] Shape025  label="R18_R_Axial_DIN0207_L63mm_D25mm_P1016mm_Horizontal_3c62972e58e7"
  Placement = pos=(12.7,-13.97,0) rot=(0,0,1;0rad)
  shape: bbox 10.96 x 2.706 x 5.603 mm, 17 faces (baked)
FEATURE [Part::Feature] Shape026  label="D5_LED_D5.0mm_60034bc3a21b"
  Placement = pos=(34.29,-35.555,0) rot=(0,0,-1;1.5708rad)
  shape: bbox 5.8 x 5.4 x 14.1 mm, 16 faces (baked)
FEATURE [Part::Feature] Shape027  label="C1_CP_Radial_D50mm_P250mm_23c4ec5917c1"
  Placement = pos=(4.445,-38.0351,0) rot=(0,0,1;1.5708rad)
  shape: bbox 6.515 x 6.128 x 7 mm, 49 faces (baked)
FEATURE [Part::Feature] Shape028  label="C2_CP_Radial_D50mm_P250mm_5b7aa9b1d5d5"
  Placement = pos=(59.182,-8.82511,0) rot=(0,0,1;1.5708rad)
  shape: bbox 6.515 x 6.128 x 7 mm, 49 faces (baked)
FEATURE [Part::Feature] Shape029  label="R21_R_Axial_DIN0207_L63mm_D25mm_P1016mm_Horizontal_043bab5f4419"
  Placement = pos=(66.675,-5.715,0) rot=(0,0,1;0rad)
  shape: bbox 10.96 x 2.706 x 5.603 mm, 17 faces (baked)
FEATURE [Part::Feature] Shape030  label="C5_CP_Radial_D50mm_P250mm_fa609370bd94"
  Placement = pos=(5.715,-26.0999,0) rot=(0,0,-1;1.5708rad)
  shape: bbox 6.515 x 6.128 x 7 mm, 49 faces (baked)
FEATURE [Part::Feature] Shape031  label="R6_R_Axial_DIN0207_L63mm_D25mm_P1016mm_Horizontal_0dea557aebe9"
  Placement = pos=(25.4,-22.86,0) rot=(0,0,-1;1.5708rad)
  shape: bbox 2.706 x 10.96 x 5.603 mm, 17 faces (baked)
FEATURE [Part::Feature] Shape032  label="R7_R_Axial_DIN0207_L63mm_D25mm_P1016mm_Horizontal_5a96a4f1f65e"
  Placement = pos=(15.24,-22.86,0) rot=(0,0,-1;1.5708rad)
  shape: bbox 2.706 x 10.96 x 5.603 mm, 17 faces (baked)
FEATURE [Part::Feature] Shape033  label="R4_R_Axial_DIN0207_L63mm_D25mm_P1016mm_Horizontal_78e21f6ad2d1"
  Placement = pos=(45.72,-22.86,0) rot=(0,0,-1;1.5708rad)
  shape: bbox 2.706 x 10.96 x 5.603 mm, 17 faces (baked)
FEATURE [Part::Feature] Shape034  label="Q4_TO-92_Wide_d99fa3e43c21"
  Placement = pos=(39.155,-30.47,0) rot=(0,0,-1;1.5708rad)
  shape: bbox 4.06 x 5.62 x 9.8 mm, 31 faces (baked)
FEATURE [Part::Feature] Shape035  label="R16_R_Axial_DIN0207_L63mm_D25mm_P1016mm_Horizontal_4811e6ad3072"
  Placement = pos=(4.445,-13.335,0) rot=(0,0,-1;1.5708rad)
  shape: bbox 2.706 x 10.96 x 5.603 mm, 17 faces (baked)
FEATURE [Part::Feature] Shape036  label="C3_CP_Radial_D50mm_P250mm_dfde33150532"
  Placement = pos=(37.465,-8.89,0) rot=(0,0,1;0rad)
  shape: bbox 6.128 x 6.515 x 7 mm, 49 faces (baked)
FEATURE [Part::Feature] Shape037  label="J3_PinHeader_1x02_P254mm_Vertical_e5993ac934dd"
  Placement = pos=(4.445,-8.26,0) rot=(0,0,1;3.14159rad)
  shape: bbox 2.54 x 5.08 x 11.54 mm, 52 faces (baked)
FEATURE [Part::Feature] Shape038  label="R9_R_Axial_DIN0207_L63mm_D25mm_P1016mm_Horizontal_532797f5b529"
  Placement = pos=(62.865,-29.845,0) rot=(0,0,1;1.5708rad)
  shape: bbox 2.706 x 10.96 x 5.603 mm, 17 faces (baked)
FEATURE [Part::Feature] Shape039  label="D9_D_A-405_P7.62mm_Horizontal_a4ace171a1cc"
  Placement = pos=(53.34,-17.145,0) rot=(0,0,1;0rad)
  shape: bbox 8.368 x 2.72 x 5.71 mm, 15 faces (baked)
FEATURE [Part::Feature] Shape040  label="R19_R_Axial_DIN0207_L63mm_D25mm_P1016mm_Horizontal_3230d582ee0a"
  Placement = pos=(25.4,-3.81,0) rot=(0,0,-1;1.5708rad)
  shape: bbox 2.706 x 10.96 x 5.603 mm, 17 faces (baked)
FEATURE [Part::Feature] Shape041  label="R10_R_Axial_DIN0207_L63mm_D25mm_P1016mm_Horizontal_891c64406b5c"
  Placement = pos=(52.705,-29.845,0) rot=(0,0,1;1.5708rad)
  shape: bbox 2.706 x 10.96 x 5.603 mm, 17 faces (baked)
FEATURE [Part::Feature] Shape042  label="R17_R_Axial_DIN0207_L63mm_D25mm_P1016mm_Horizontal_3e8b808dfa95"
  Placement = pos=(40.132,-12.7,0) rot=(0,0,1;0rad)
  shape: bbox 10.96 x 2.706 x 5.603 mm, 17 faces (baked)
FEATURE [Part::Feature] Shape043  label="Q3_TO-92_Wide_e69642412aa5"
  Placement = pos=(49.315,-30.47,0) rot=(0,0,-1;1.5708rad)
  shape: bbox 4.06 x 5.62 x 9.8 mm, 31 faces (baked)
FEATURE [Part::Feature] Shape044  label="D2_LED_D5.0mm_370cab26fe4a"
  Placement = pos=(64.77,-35.555,0) rot=(0,0,-1;1.5708rad)
  shape: bbox 5.8 x 5.4 x 14.1 mm, 16 faces (baked)
FEATURE [Part::Feature] Shape045  label="Q10_TO-92_Wide_6694c14d1b8c"
  Placement = pos=(33.87,-11.44,0) rot=(0,0,1;1.5708rad)
  shape: bbox 4.06 x 5.62 x 9.8 mm, 31 faces (baked)
FEATURE [Part::Feature] Shape046  label="D7_LED_D5.0mm_994bed6c4edc"
  Placement = pos=(13.97,-35.56,0) rot=(0,0,-1;1.5708rad)
  shape: bbox 5.8 x 5.4 x 14.1 mm, 16 faces (baked)
FEATURE [Part::Feature] Shape047  label="D8_D_A-405_P7.62mm_Horizontal_a44a823cf9d3"
  Placement = pos=(63.5,-17.145,0) rot=(0,0,1;0rad)
  shape: bbox 8.368 x 2.72 x 5.71 mm, 15 faces (baked)
FEATURE [Part::Feature] Shape048  label="R11_R_Axial_DIN0207_L63mm_D25mm_P1016mm_Horizontal_5143b20dbc7e"
  Placement = pos=(42.545,-29.845,0) rot=(0,0,1;1.5708rad)
  shape: bbox 2.706 x 10.96 x 5.603 mm, 17 faces (baked)
FEATURE [Part::Feature] Shape049  label="Q2_TO-92_Wide_83d40f09d7ee"
  Placement = pos=(59.475,-30.47,0) rot=(0,0,-1;1.5708rad)
  shape: bbox 4.06 x 5.62 x 9.8 mm, 31 faces (baked)
FEATURE [Part::Feature] Shape050  label="D10_D_A-405_P7.62mm_Horizontal_c6f234e0c10f"
  Placement = pos=(43.18,-17.145,0) rot=(0,0,1;0rad)
  shape: bbox 8.368 x 2.72 x 5.71 mm, 15 faces (baked)
FEATURE [Part::Feature] Shape051  label="R23_R_Axial_DIN0207_L63mm_D25mm_P1016mm_Horizontal_4c4d199288b2"
  Placement = pos=(28.575,-13.97,0) rot=(0,0,1;1.5708rad)
  shape: bbox 2.706 x 10.96 x 5.603 mm, 17 faces (baked)
FEATURE [Part::Feature] Shape052  label="D1_LED_D5.0mm_5167b579a80a"
  Placement = pos=(74.93,-35.555,0) rot=(0,0,-1;1.5708rad)
  shape: bbox 5.8 x 5.4 x 14.1 mm, 16 faces (baked)
FEATURE [Part::Feature] Shape053  label="C4_CP_Radial_D50mm_P250mm_2689a81529ee"
  Placement = pos=(19.7499,-8.255,0) rot=(0,0,1;0rad)
  shape: bbox 6.128 x 6.515 x 7 mm, 49 faces (baked)
FEATURE [Part::Feature] Shape054  label="R5_R_Axial_DIN0207_L63mm_D25mm_P1016mm_Horizontal_431b73a015bb"
  Placement = pos=(35.56,-22.86,0) rot=(0,0,-1;1.5708rad)
  shape: bbox 2.706 x 10.96 x 5.603 mm, 17 faces (baked)
FEATURE [Part::Feature] Shape055  label="D13_D_A-405_P7.62mm_Horizontal_4916f0710787"
  Placement = pos=(12.7,-17.145,0) rot=(0,0,1;0rad)
  shape: bbox 8.368 x 2.72 x 5.71 mm, 15 faces (baked)
FEATURE [App::Part] Top_1d7d
  Group = -> [Shape,Shape001,Shape002,Shape003,Shape004,Shape005,Shape006,Shape007,Shape008,Shape009,Shape010,Shape011,Shape012,Shape013,Shape014,Shape015,Shape016,Shape017,Shape018,Shape019,Shape020,Shape021,Shape022,Shape023,Shape024,Shape025,Shape026,Shape027,Shape028,Shape029,Shape030,Shape031,Shape032,Shape033,Shape034,Shape035,Shape036,Shape037,Shape038,Shape039,Shape040,Shape041,Shape042,Shape043,+12 more]
  Origin = -> Origin011
FEATURE [App::Part] Step_Models_1d7d
  Group = -> [Top_1d7d]
  Origin = -> Origin010
FEATURE [App::Part] Board_1d7d  label="PMG"
  Group = -> [Local_CS_1d7d,Board_Geoms_1d7d,Step_Models_1d7d]
  Origin = -> Origin009
FEATURE [Sketcher::SketchObject] Sketch010
  AttachmentOffset = pos=(0,0,13) rot=(0,0,1;0rad)
  FullyConstrained = true
  MapMode = 5
  Placement = pos=(0,0,13) rot=(0,0,1;0rad)
  Support = -> [XY_Plane003]
  expr: .AttachmentOffset.Base.z = <<Parameter>>.Height + <<Parameter>>.Offset
  sketch-geometry (8):
    g0: Circle CenterX=12.99 CenterY=-6.99 CenterZ=0 NormalX=0 NormalY=0 NormalZ=1 AngleXU=0 Radius=4.85
    g1: Circle CenterX=13.97 CenterY=-36.83 CenterZ=0 NormalX=0 NormalY=0 NormalZ=1 AngleXU=0 Radius=2.55
    g2: Circle CenterX=24.13 CenterY=-36.83 CenterZ=0 NormalX=0 NormalY=0 NormalZ=1 AngleXU=0 Radius=2.55
    g3: Circle CenterX=34.29 CenterY=-36.83 CenterZ=0 NormalX=0 NormalY=0 NormalZ=1 AngleXU=0 Radius=2.55
    g4: Circle CenterX=44.45 CenterY=-36.83 CenterZ=0 NormalX=0 NormalY=0 NormalZ=1 AngleXU=0 Radius=2.55
    g5: Circle CenterX=54.61 CenterY=-36.83 CenterZ=0 NormalX=0 NormalY=0 NormalZ=1 AngleXU=0 Radius=2.55
    g6: Circle CenterX=64.77 CenterY=-36.83 CenterZ=0 NormalX=0 NormalY=0 NormalZ=1 AngleXU=0 Radius=2.55
    g7: Circle CenterX=74.93 CenterY=-36.83 CenterZ=0 NormalX=0 NormalY=0 NormalZ=1 AngleXU=0 Radius=2.55
  constraints (24):
    c: Diameter(g1) = 5.1
    c: Equal(g1,g2)
    c: Equal(g2,g3)
    c: Equal(g3,g4)
    c: Equal(g4,g5)
    c: Equal(g5,g6)
    c: Equal(g6,g7)
    c: Horizontal(g1,g2)
    c: Horizontal(g2,g3)
    c: Horizontal(g3,g4)
    c: Horizontal(g4,g5)
    c: Horizontal(g5,g6)
    c: Horizontal(g6,g7)
    c: DistanceY(g1,g-1) = 36.83
    c: DistanceX(g-1,g1) = 13.97
    c: DistanceX(g1,g2) = 10.16
    c: DistanceX(g2,g3) = 10.16
    c: DistanceX(g3,g4) = 10.16
    c: DistanceX(g4,g5) = 10.16
    c: DistanceX(g5,g6) = 10.16
    c: DistanceX(g6,g7) = 10.16
    c: Diameter(g0) = 9.7
    c: DistanceX(g-1,g0) = 12.99
    c: DistanceY(g0,g-1) = 6.99
FEATURE [PartDesign::Pocket] Pocket009
  BaseFeature = -> Pad001
  Direction = (0,0,-1)
  Length = 1.5
  Length2 = 5
  Profile = -> Sketch010
  ReferenceAxis = -> Sketch010 [N_Axis]
  Refine = true
  Type = 0
  expr: Length = <<Parameter>>.Inlay_Height
FEATURE [PartDesign::Body] Body001  label="AcrylGlass"
  Group = -> [Sketch007,Pad001,Sketch010,Pocket009]
  Origin = -> Origin003
  Tip = -> Pocket009
FEATURE [App::Part] Part001  label="Part_Cover"
  Group = -> [Body001]
  Origin = -> Origin002
FEATURE [TechDraw::DrawViewPart] View
  CoarseView = false
  Direction = (0,0,1)
  Focus = 100
  HardHidden = false
  IsoCount = 0
  IsoHidden = false
  IsoVisible = false
  LockPosition = false
  Perspective = false
  Rotation = 180
  ScaleType = 0
  SeamHidden = false
  SeamVisible = true
  SmoothHidden = false
  SmoothVisible = true
  Source = -> [Part001]
  X = 143.792
  XDirection = (-1,0,0)
  Y = 120.101
FEATURE [TechDraw::DrawViewDimension] Dimension012
  AngleOverride = false
  Arbitrary = false
  ArbitraryTolerances = false
  EqualTolerance = true
  ExtensionAngle = 0
  FormatSpec = %.2w
  FormatSpecOverTolerance = %+.2w
  FormatSpecUnderTolerance = %+.2w
  Inverted = false
  LineAngle = 0
  LockPosition = false
  MeasureType = 1
  OverTolerance = 0
  References2D = -> [View]
  Rotation = 0
  ScaleType = 0
  TheoreticalExact = false
  Type = 1
  UnderTolerance = 0
  X = 0.331754
  Y = 45.0924
FEATURE [TechDraw::DrawViewDimension] Dimension013
  AngleOverride = false
  Arbitrary = false
  ArbitraryTolerances = false
  EqualTolerance = true
  ExtensionAngle = 0
  FormatSpec = %.2w
  FormatSpecOverTolerance = %+.2w
  FormatSpecUnderTolerance = %+.2w
  Inverted = false
  LineAngle = 0
  LockPosition = false
  MeasureType = 1
  OverTolerance = 0
  References2D = -> [View]
  Rotation = 0
  ScaleType = 0
  TheoreticalExact = false
  Type = 2
  UnderTolerance = 0
  X = -68.6727
  Y = 1.44141
FEATURE [TechDraw::DrawPage] Page001  label="Page_Cover"
  KeepUpdated = true
  NextBalloonIndex = 1
  ProjectionType = 0
  Template = -> Template001
  Views = -> [View,Dimension012,Dimension013,Sheet]
FEATURE [Part::Feature] trajectory_line
  shape: bbox 2e-07 x 2e-07 x 40 mm, 0 faces, 0 solids (baked)
FEATURE [App::DocumentObjectGroupPython] SimpleGroup  # scripted group (container) (typed FeaturePython)
  AnimationStepTime = 0.01
  AnimationSteps = 20
  Distance = 40
  Group = -> [trajectory_line]
  Revolutions = 0
FEATURE [Part::Feature] trajectory_line001
  shape: bbox 20 x 2e-07 x 2e-07 mm, 0 faces, 0 solids (baked)
FEATURE [App::DocumentObjectGroupPython] SimpleGroup001  # scripted group (container) (typed FeaturePython)
  AnimationStepTime = 0
  AnimationSteps = 20
  Distance = 20
  Group = -> [trajectory_line001]
  Revolutions = 0
FEATURE [Part::Feature] trajectory_line002
  shape: bbox 2e-07 x 2e-07 x 20 mm, 0 faces, 0 solids (baked)
FEATURE [App::DocumentObjectGroupPython] SimpleGroup002  # scripted group (container) (typed FeaturePython)
  AnimationStepTime = 0.01
  AnimationSteps = 20
  Distance = 30
  Group = -> [trajectory_line002]
  Revolutions = 0
FEATURE [App::DocumentObjectGroupPython] ExplodedAssembly  # scripted group (container) (typed FeaturePython)
  AnimationStep = 0
  CurrentTrajectory = 0
  Group = -> [SimpleGroup,SimpleGroup001,SimpleGroup002]
  InAnimation = false
  RemoveAllTrajectories = false
  ResetAnimation = false
note: 2 file-system paths scrubbed to <path> (originals preserved in the JSON sidecar)
